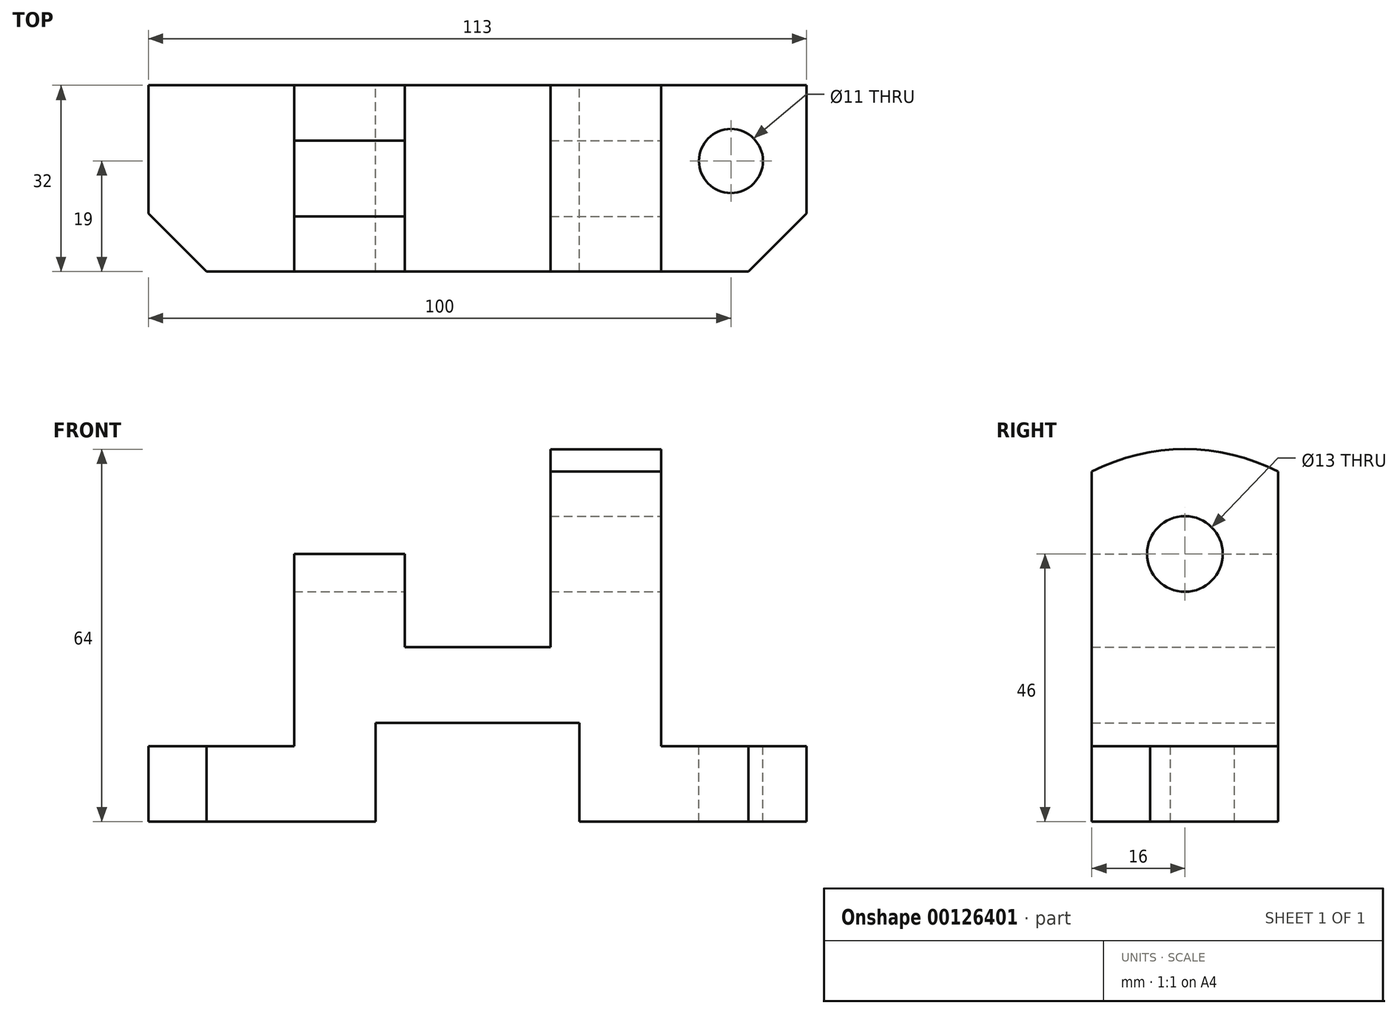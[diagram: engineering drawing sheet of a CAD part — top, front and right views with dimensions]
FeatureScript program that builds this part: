
annotation { "Feature Type Name" : "Feature", "Feature Type Description" : "" }
export const myFeature = defineFeature(function(context is Context, id is Id, definition is map)
    precondition{}
    {
        {
            var Q0;
            Q0=qCreatedBy(makeId("Front.planeOp"),FACE);
            var sketch = newSketch(context, id + "F0", { "sketchPlane" : qUnion([Q0])});
            skLineSegment(sketch, "E0", {"start": v(-56.5, 0) * mm, "end": v(-17.5, 0) * mm});
            skLineSegment(sketch, "E1", {"start": v(-17.5, 0) * mm, "end": v(-17.5, 17) * mm});
            skLineSegment(sketch, "E2", {"start": v(-17.5, 17) * mm, "end": v(0, 17) * mm});
            skLineSegment(sketch, "E3", {"start": v(0, 17) * mm, "end": v(17.5, 17) * mm});
            skLineSegment(sketch, "E4", {"start": v(17.5, 17) * mm, "end": v(17.5, 0) * mm});
            skLineSegment(sketch, "E5", {"start": v(17.5, 0) * mm, "end": v(56.5, 0) * mm});
            skLineSegment(sketch, "E6", {"start": v(56.5, 0) * mm, "end": v(56.5, 13) * mm});
            skLineSegment(sketch, "E7", {"start": v(56.5, 13) * mm, "end": v(31.5, 13) * mm});
            skLineSegment(sketch, "E8", {"start": v(31.5, 13) * mm, "end": v(31.5, 46) * mm});
            skLineSegment(sketch, "E9", {"start": v(31.5, 46) * mm, "end": v(12.5, 46) * mm});
            skLineSegment(sketch, "E10", {"start": v(12.5, 46) * mm, "end": v(12.5, 30) * mm});
            skLineSegment(sketch, "E11", {"start": v(-12.5, 30) * mm, "end": v(-12.5, 46) * mm});
            skLineSegment(sketch, "E12", {"start": v(-12.5, 46) * mm, "end": v(-31.5, 46) * mm});
            skLineSegment(sketch, "E13", {"start": v(-31.5, 46) * mm, "end": v(-31.5, 13) * mm});
            skLineSegment(sketch, "E14", {"start": v(-31.5, 13) * mm, "end": v(-56.5, 13) * mm});
            skLineSegment(sketch, "E15", {"start": v(-56.5, 13) * mm, "end": v(-56.5, 0) * mm});
            skLineSegment(sketch, "E16", {"start": v(12.5, 30) * mm, "end": v(0, 30) * mm});
            skLineSegment(sketch, "E17", {"start": v(0, 30) * mm, "end": v(-12.5, 30) * mm});
            skSolve(sketch);
        }
        {
            var Q0;
            Q0 = qSketchRegion(id + "F0", true);
            extrude(context, id + "F1", {"entities" : qUnion([Q0]), "endBound" : BoundingType.SYMMETRIC, "depth" : 32 * mm});
        }
        {
            var Q0;
            Q0=makeQuery(id+"F1.opExtrude","SWEPT_FACE",FACE,{"disambiguationData":[OSD([sQuery(id+"F0.wireOp",EDGE,"E8")])]});
            var sketch = newSketch(context, id + "F2", { "sketchPlane" : qUnion([Q0])});
            skCircle(sketch, "E18", {"center": v(0, 46) * mm, "radius": 6.5 * mm});
            skLineSegment(sketch, "E19", {"start": v(-16, 46) * mm, "end": v(-16, 60.13) * mm});
            skLineSegment(sketch, "E20", {"start": v(16, 46) * mm, "end": v(16, 60.13) * mm});
            skArc(sketch, "E21", {"start": v(-16, 60.13) * mm, "mid": v(0, 64) * mm, "end": v(16, 60.13) * mm});
            skLineSegment(sketch, "E22", {"start": v(16, 46) * mm, "end": v(6.5, 46) * mm});
            skLineSegment(sketch, "E23", {"start": v(-16, 46) * mm, "end": v(-6.5, 46) * mm});
            skSolve(sketch);
        }
        {
            var Q0;
            Q0 = qSketchRegion(id + "F2", true);
            extrude(context, id + "F3", {"entities" : qUnion([Q0]), "operationType" : NewBodyOperationType.ADD, "oppositeDirection" : true, "depth" : 19 * mm});
        }
        {
            var Q0;
            {var subQ0=sQuery(id+"F2.wireOp",EDGE,"E18");var subQ1=makeQuery(id+"F1.opExtrude","SWEPT_EDGE",EDGE,{"disambiguationData":[OSD([sQuery(id+"F0.wireOp",EDGE,"E8"),sQuery(id+"F0.wireOp",EDGE,"E9")])]});var subQ2=makeQuery(id+"F2.imprint","INTERSECT",VERTEX,{"derivedFrom":[subQ1,subQ0,sQuery(id+"F2.wireOp",EDGE,"E22")]});Q0=makeQuery(id+"F2.imprint","IMPRINT",FACE,{"disambiguationData":[TD([[makeQuery(id+"F2.imprint","IMPRINT",EDGE,{"disambiguationData":[TD([[subQ2,-1.0]])],"derivedFrom":subQ0}),1.0]])]});}
            var Q1;
            {var subQ0=sQuery(id+"F2.wireOp",EDGE,"E18");var subQ1=makeQuery(id+"F1.opExtrude","SWEPT_EDGE",EDGE,{"disambiguationData":[OSD([sQuery(id+"F0.wireOp",EDGE,"E8"),sQuery(id+"F0.wireOp",EDGE,"E9")])]});var subQ2=makeQuery(id+"F2.imprint","INTERSECT",VERTEX,{"derivedFrom":[subQ1,subQ0,sQuery(id+"F2.wireOp",EDGE,"E22")]});Q1=makeQuery(id+"F2.imprint","IMPRINT",FACE,{"disambiguationData":[TD([[makeQuery(id+"F2.imprint","IMPRINT",EDGE,{"disambiguationData":[TD([[subQ2,1.0]])],"derivedFrom":subQ0}),1.0]])]});}
            extrude(context, id + "F4", {"entities" : qUnion([Q0, Q1]), "operationType" : NewBodyOperationType.REMOVE, "endBound" : BoundingType.THROUGH_ALL, "oppositeDirection" : true, "depth" : 25 * mm});
        }
        {
            var Q0;
            Q0=makeQuery(id+"F1.opExtrude","CAP_EDGE",EDGE,{"disambiguationData":[OSD([sQuery(id+"F0.wireOp",EDGE,"E6")])],"isStart":false});
            var Q1;
            Q1=makeQuery(id+"F1.opExtrude","CAP_EDGE",EDGE,{"disambiguationData":[OSD([sQuery(id+"F0.wireOp",EDGE,"E15")])],"isStart":false});
            chamfer(context, id + "F5", {"entities" : qUnion([Q0, Q1]), "width" : 10 * mm, "tangentPropagation" : true});
        }
        {
            var Q0;
            Q0=makeQuery(id+"F1.opExtrude","SWEPT_FACE",FACE,{"disambiguationData":[OSD([sQuery(id+"F0.wireOp",EDGE,"E7")])]});
            var sketch = newSketch(context, id + "F6", { "sketchPlane" : qUnion([Q0])});
            skCircle(sketch, "E24", {"center": v(43.5, 3) * mm, "radius": 5.5 * mm});
            skSolve(sketch);
        }
        {
            var Q0;
            Q0 = qSketchRegion(id + "F6", true);
            extrude(context, id + "F7", {"entities" : qUnion([Q0]), "operationType" : NewBodyOperationType.REMOVE, "endBound" : BoundingType.THROUGH_ALL, "oppositeDirection" : true, "depth" : 25 * mm});
        }
    });
